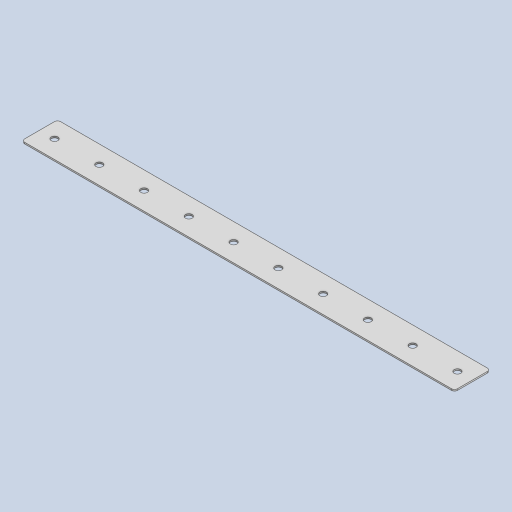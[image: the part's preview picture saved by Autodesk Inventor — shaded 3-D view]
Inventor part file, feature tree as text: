
AUTODESK INVENTOR PART (.ipt)
format: ipt  version: 2023 (Build 270158000, 158)  size: 114,688 bytes
history: native  units: in
note: dims shown in document units (in); Inventor stores cm internally (conversion verified against a paired STEP export)
features: other x1, extrude x1, fillet x1, sketch x1
ambient origin geometry x8: Origin, YZ Plane, XZ Plane, XY Plane, X Axis, Y Axis, Z Axis, Center Point
bodies: Body1 (feature_tree)
feature tree (4):
  other  "ソリッド1"
  extrude  "押し出し1"  Depth=5.7087in
  fillet  "フィレット1"  Radius=0.4724in
  sketch  "スケッチ1"
